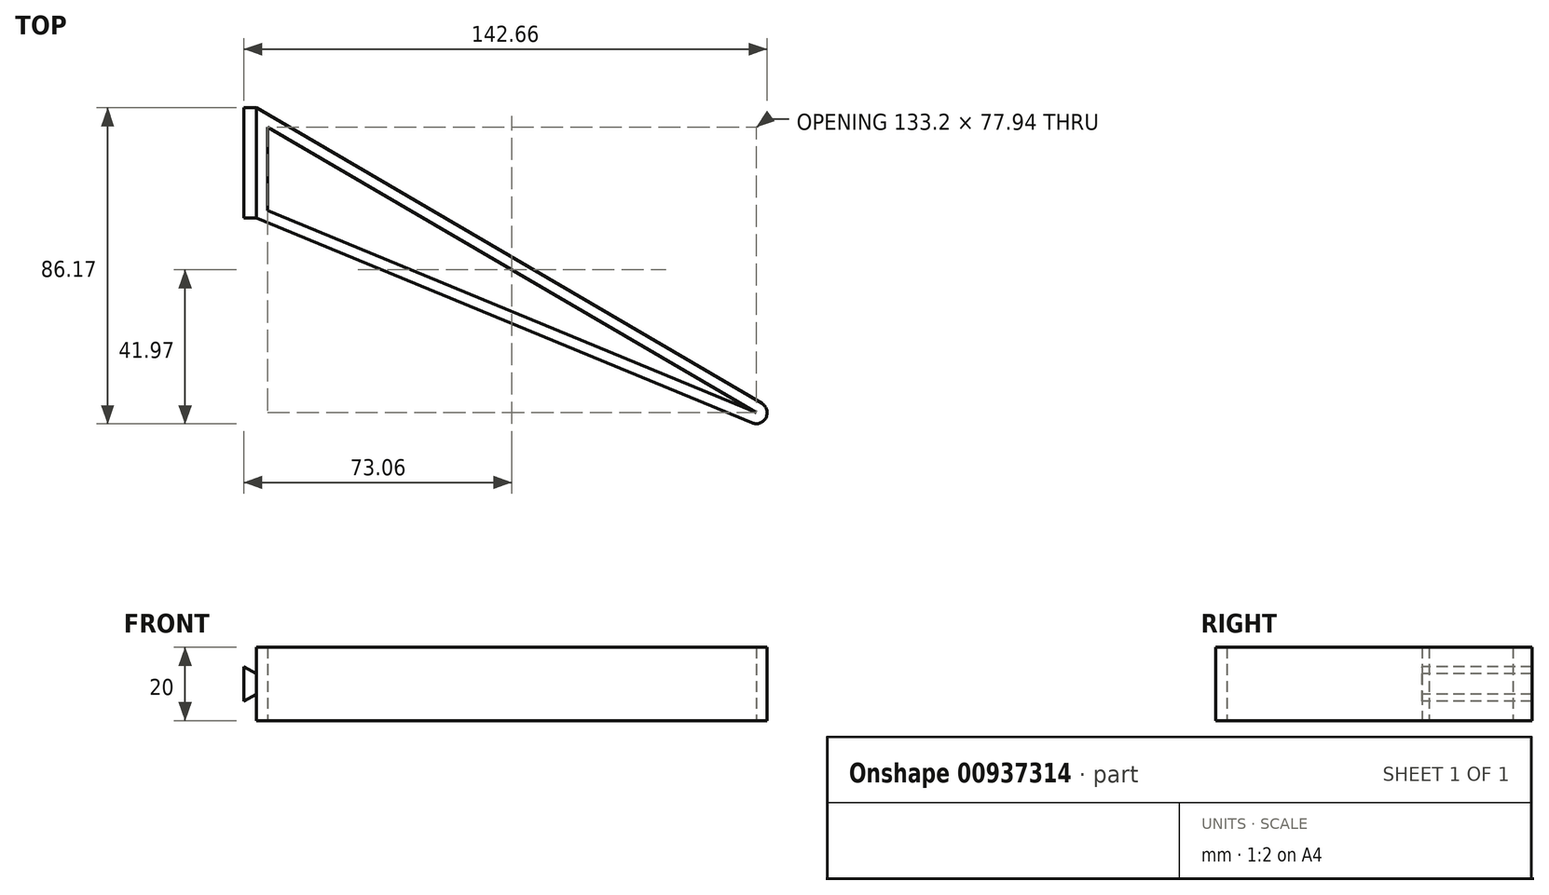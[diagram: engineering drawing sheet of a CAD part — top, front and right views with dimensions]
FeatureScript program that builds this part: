
annotation { "Feature Type Name" : "Feature", "Feature Type Description" : "" }
export const myFeature = defineFeature(function(context is Context, id is Id, definition is map)
    precondition{}
    {
        {
            var Q0;
            Q0=qCreatedBy(makeId("Top.planeOp"),FACE);
            var sketch = newSketch(context, id + "F0", { "sketchPlane" : qUnion([Q0])});
            skLineSegment(sketch, "E0", {"start": v(0, 0) * mm, "end": v(0, 30) * mm});
            skLineSegment(sketch, "E1", {"start": v(0, 0) * mm, "end": v(135.05, -55.94) * mm});
            skLineSegment(sketch, "E2", {"start": v(0, 30) * mm, "end": v(137.71, -50.58) * mm});
            skArc(sketch, "E3", {"start": v(135.05, -55.94) * mm, "mid": v(138.89, -54.5) * mm, "end": v(137.71, -50.58) * mm});
            skPoint(sketch, "E4.orphan", {"position": v(175.54, -72.7) * mm});
            skLineSegment(sketch, "E5.0", {"start": v(3, 24.77) * mm, "end": v(136.2, -53.17) * mm});
            skLineSegment(sketch, "E5.1", {"start": v(3, 2) * mm, "end": v(3, 24.77) * mm});
            skLineSegment(sketch, "E5.2", {"start": v(3, 2) * mm, "end": v(136.2, -53.17) * mm});
            skSolve(sketch);
        }
        {
            var Q0;
            Q0=makeQuery(id+"F0.imprint","IMPRINT",FACE,{"disambiguationData":[TD([[makeQuery(id+"F0.imprint","IMPRINT",EDGE,{"derivedFrom":sQuery(id+"F0.wireOp",EDGE,"E0")}),-1.0]])]});
            extrude(context, id + "F1", {"entities" : qUnion([Q0]), "depth" : 20 * mm, "offsetDistance" : 25 * mm});
        }
        {
            var Q0;
            Q0=qCreatedBy(makeId("Front.planeOp"),FACE);
            var sketch = newSketch(context, id + "F2", { "sketchPlane" : qUnion([Q0])});
            skLineSegment(sketch, "E6", {"start": v(0, 12.75) * mm, "end": v(0, 7.25) * mm});
            skLineSegment(sketch, "E7", {"start": v(0, 7.25) * mm, "end": v(-3.46, 5.25) * mm});
            skLineSegment(sketch, "E8", {"start": v(-3.46, 5.25) * mm, "end": v(-3.46, 14.75) * mm});
            skLineSegment(sketch, "E9", {"start": v(-3.46, 14.75) * mm, "end": v(0, 12.75) * mm});
            skSolve(sketch);
        }
        {
            var Q0;
            Q0=makeQuery(id+"F2.imprint","IMPRINT",FACE,{"disambiguationData":[TD([[makeQuery(id+"F2.imprint","IMPRINT",EDGE,{"derivedFrom":sQuery(id+"F2.wireOp",EDGE,"E6")}),-1.0]])]});
            extrude(context, id + "F3", {"entities" : qUnion([Q0]), "operationType" : NewBodyOperationType.ADD, "oppositeDirection" : true, "depth" : 30 * mm, "offsetDistance" : 25 * mm});
        }
    });
